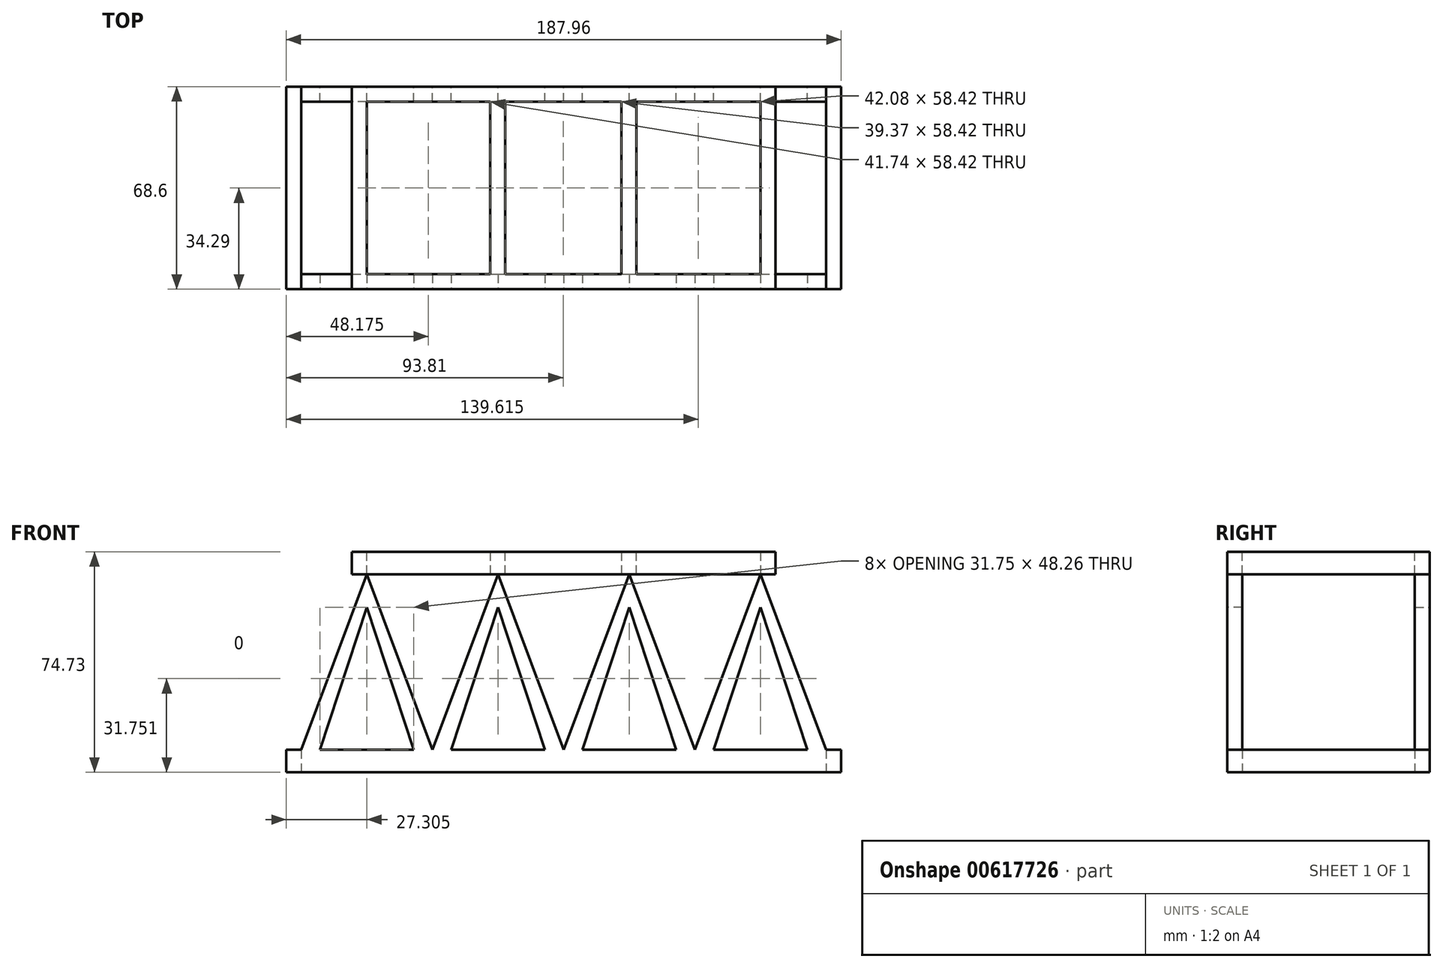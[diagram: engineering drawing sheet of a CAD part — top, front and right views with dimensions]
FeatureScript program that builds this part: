
annotation { "Feature Type Name" : "Feature", "Feature Type Description" : "" }
export const myFeature = defineFeature(function(context is Context, id is Id, definition is map)
    precondition{}
    {
        {
            var Q0;
            Q0=qCreatedBy(makeId("Front.planeOp"),FACE);
            var sketch = newSketch(context, id + "F0", { "sketchPlane" : qUnion([Q0])});
            skLineSegment(sketch, "E0.bottom", {"start": v(-88.9, -35.02) * mm, "end": v(88.9, -35.02) * mm});
            skLineSegment(sketch, "E0.top", {"start": v(-88.9, -42.64) * mm, "end": v(88.9, -42.64) * mm});
            skLineSegment(sketch, "E0.left", {"start": v(-88.9, -35.02) * mm, "end": v(-88.9, -42.64) * mm});
            skLineSegment(sketch, "E0.right", {"start": v(88.9, -35.02) * mm, "end": v(88.9, -42.64) * mm});
            skLineSegment(sketch, "E1.bottom", {"start": v(-66.68, 32.09) * mm, "end": v(66.68, 32.09) * mm});
            skLineSegment(sketch, "E1.top", {"start": v(-66.68, 24.47) * mm, "end": v(66.68, 24.47) * mm});
            skLineSegment(sketch, "E1.left", {"start": v(-66.68, 32.09) * mm, "end": v(-66.68, 24.47) * mm});
            skLineSegment(sketch, "E1.right", {"start": v(66.68, 32.09) * mm, "end": v(66.68, 24.47) * mm});
            skSolve(sketch);
        }
        {
            var Q0;
            Q0 = qSketchRegion(id + "F0", true);
            extrude(context, id + "F1", {"entities" : qUnion([Q0]), "oppositeDirection" : true, "depth" : 5.08 * mm, "offsetDistance" : 25.4 * mm});
        }
        {
            var Q0;
            Q0=qCreatedBy(makeId("Front.planeOp"),FACE);
            var sketch = newSketch(context, id + "F2", { "sketchPlane" : qUnion([Q0])});
            skLineSegment(sketch, "E2", {"start": v(-88.9, -35.02) * mm, "end": v(-66.67, 24.47) * mm});
            skLineSegment(sketch, "E3", {"start": v(-66.67, 24.47) * mm, "end": v(-44.45, -35.02) * mm});
            skLineSegment(sketch, "E4", {"start": v(-44.45, -35.02) * mm, "end": v(-88.9, -35.02) * mm});
            skLineSegment(sketch, "E5", {"start": v(-44.45, -35.02) * mm, "end": v(-22.22, 24.47) * mm});
            skLineSegment(sketch, "E6", {"start": v(-22.22, 24.47) * mm, "end": v(0, -35.02) * mm});
            skLineSegment(sketch, "E7", {"start": v(0, -35.02) * mm, "end": v(22.23, 24.47) * mm});
            skLineSegment(sketch, "E8", {"start": v(22.23, 24.47) * mm, "end": v(44.45, -35.02) * mm});
            skLineSegment(sketch, "E9", {"start": v(44.45, -35.02) * mm, "end": v(66.68, 24.47) * mm});
            skLineSegment(sketch, "E10", {"start": v(66.68, 24.47) * mm, "end": v(88.9, -35.02) * mm});
            skLineSegment(sketch, "E11", {"start": v(88.9, -35.02) * mm, "end": v(44.45, -35.02) * mm});
            skLineSegment(sketch, "E12", {"start": v(44.45, -35.02) * mm, "end": v(0, -35.02) * mm});
            skLineSegment(sketch, "E13", {"start": v(0, -35.02) * mm, "end": v(-44.45, -35.02) * mm});
            skLineSegment(sketch, "E14", {"start": v(-82.55, -35.02) * mm, "end": v(-88.9, -35.02) * mm});
            skLineSegment(sketch, "E15", {"start": v(-82.55, -35.02) * mm, "end": v(-66.68, 13.24) * mm});
            skLineSegment(sketch, "E16", {"start": v(-66.68, 13.24) * mm, "end": v(-50.8, -35.02) * mm});
            skLineSegment(sketch, "E17", {"start": v(-50.8, -35.02) * mm, "end": v(-44.45, -35.02) * mm});
            skLineSegment(sketch, "E18", {"start": v(-44.45, -35.02) * mm, "end": v(-38.1, -35.02) * mm});
            skLineSegment(sketch, "E19", {"start": v(-38.1, -35.02) * mm, "end": v(-22.23, 13.24) * mm});
            skLineSegment(sketch, "E20", {"start": v(-22.23, 13.24) * mm, "end": v(-6.35, -35.02) * mm});
            skLineSegment(sketch, "E21", {"start": v(-6.35, -35.02) * mm, "end": v(0, -35.02) * mm});
            skLineSegment(sketch, "E22", {"start": v(0, -35.02) * mm, "end": v(6.35, -35.02) * mm});
            skLineSegment(sketch, "E23", {"start": v(6.35, -35.02) * mm, "end": v(22.23, 13.24) * mm});
            skLineSegment(sketch, "E24", {"start": v(22.23, 13.24) * mm, "end": v(38.1, -35.02) * mm});
            skLineSegment(sketch, "E25", {"start": v(38.1, -35.02) * mm, "end": v(44.45, -35.02) * mm});
            skLineSegment(sketch, "E26", {"start": v(44.45, -35.02) * mm, "end": v(50.8, -35.02) * mm});
            skLineSegment(sketch, "E27", {"start": v(50.8, -35.02) * mm, "end": v(66.68, 13.24) * mm});
            skLineSegment(sketch, "E28", {"start": v(66.68, 13.24) * mm, "end": v(82.55, -35.02) * mm});
            skLineSegment(sketch, "E29", {"start": v(82.55, -35.02) * mm, "end": v(88.9, -35.02) * mm});
            skSolve(sketch);
        }
        {
            var Q0;
            Q0=makeQuery(id+"F2.imprint","IMPRINT",FACE,{"disambiguationData":[TD([[makeQuery(id+"F2.imprint","IMPRINT",EDGE,{"derivedFrom":sQuery(id+"F2.wireOp",EDGE,"E2")}),-1.0]])]});
            var Q1;
            Q1=makeQuery(id+"F2.imprint","IMPRINT",FACE,{"disambiguationData":[TD([[makeQuery(id+"F2.imprint","IMPRINT",EDGE,{"derivedFrom":sQuery(id+"F2.wireOp",EDGE,"E5")}),-1.0]])]});
            var Q2;
            Q2=makeQuery(id+"F2.imprint","IMPRINT",FACE,{"disambiguationData":[TD([[makeQuery(id+"F2.imprint","IMPRINT",EDGE,{"derivedFrom":sQuery(id+"F2.wireOp",EDGE,"E7")}),-1.0]])]});
            var Q3;
            Q3=makeQuery(id+"F2.imprint","IMPRINT",FACE,{"disambiguationData":[TD([[makeQuery(id+"F2.imprint","IMPRINT",EDGE,{"derivedFrom":sQuery(id+"F2.wireOp",EDGE,"E9")}),-1.0]])]});
            extrude(context, id + "F3", {"entities" : qUnion([Q0, Q1, Q2, Q3]), "operationType" : NewBodyOperationType.ADD, "oppositeDirection" : true, "depth" : 5.08 * mm, "offsetDistance" : 25.4 * mm});
        }
        {
            var Q0;
            Q0=makeQuery(id+"F1.opExtrude","SWEPT_FACE",FACE,{"disambiguationData":[OSD([sQuery(id+"F0.wireOp",EDGE,"E0.left")])]});
            var sketch = newSketch(context, id + "F4", { "sketchPlane" : qUnion([Q0])});
            skLineSegment(sketch, "E30", {"start": v(0, -42.64) * mm, "end": v(0, -35.02) * mm});
            skLineSegment(sketch, "E31", {"start": v(0, -35.02) * mm, "end": v(-63.5, -35.02) * mm});
            skLineSegment(sketch, "E32", {"start": v(-63.5, -35.02) * mm, "end": v(-63.5, -42.64) * mm});
            skLineSegment(sketch, "E33", {"start": v(-63.5, -42.64) * mm, "end": v(0, -42.64) * mm});
            skSolve(sketch);
        }
        {
            var Q0;
            {var subQ2=sQuery(id+"F4.wireOp",EDGE,"E32");Q0=makeQuery(id+"F4.imprint","IMPRINT",FACE,{"disambiguationData":[TD([[makeQuery(id+"F4.imprint","IMPRINT",EDGE,{"derivedFrom":subQ2}),1.0]])]});}
            var Q1;
            {var subQ0=sQuery(id+"F4.wireOp",EDGE,"E30");Q1=makeQuery(id+"F4.imprint","IMPRINT",FACE,{"disambiguationData":[TD([[makeQuery(id+"F4.imprint","IMPRINT",EDGE,{"derivedFrom":subQ0}),-1.0]])]});}
            extrude(context, id + "F5", {"entities" : qUnion([Q0, Q1]), "operationType" : NewBodyOperationType.ADD, "depth" : 5.08 * mm, "offsetDistance" : 25.4 * mm});
        }
        {
            var Q0;
            Q0=makeQuery(id+"F5.opExtrude","SWEPT_FACE",FACE,{"disambiguationData":[OSD([sQuery(id+"F4.wireOp",EDGE,"E32")])]});
            var sketch = newSketch(context, id + "F6", { "sketchPlane" : qUnion([Q0])});
            skLineSegment(sketch, "E34", {"start": v(93.98, -42.64) * mm, "end": v(-88.9, -42.64) * mm});
            skLineSegment(sketch, "E35", {"start": v(93.98, -42.64) * mm, "end": v(93.98, -35.02) * mm});
            skLineSegment(sketch, "E36", {"start": v(93.98, -35.02) * mm, "end": v(-88.9, -35.02) * mm});
            skLineSegment(sketch, "E37", {"start": v(-88.9, -35.02) * mm, "end": v(-88.9, -42.64) * mm});
            skSolve(sketch);
        }
        {
            var Q0;
            Q0 = qSketchRegion(id + "F6", true);
            extrude(context, id + "F7", {"entities" : qUnion([Q0]), "operationType" : NewBodyOperationType.ADD, "depth" : 5.08 * mm, "offsetDistance" : 25.4 * mm});
        }
        {
            var Q0;
            Q0=makeQuery(id+"F1.opExtrude","SWEPT_FACE",FACE,{"disambiguationData":[OSD([sQuery(id+"F0.wireOp",EDGE,"E0.right")])]});
            var sketch = newSketch(context, id + "F8", { "sketchPlane" : qUnion([Q0])});
            skLineSegment(sketch, "E38", {"start": v(0, -42.64) * mm, "end": v(0, -35.02) * mm});
            skLineSegment(sketch, "E39", {"start": v(0, -42.64) * mm, "end": v(68.6, -42.64) * mm});
            skPoint(sketch, "E39.endSnap0", {"position": v(2.54, -42.64) * mm});
            skLineSegment(sketch, "E40", {"start": v(68.6, -42.64) * mm, "end": v(68.6, -35.02) * mm});
            skLineSegment(sketch, "E41", {"start": v(68.6, -35.02) * mm, "end": v(0, -35.02) * mm});
            skSolve(sketch);
        }
        {
            var Q0;
            Q0 = qSketchRegion(id + "F8", true);
            extrude(context, id + "F9", {"entities" : qUnion([Q0]), "operationType" : NewBodyOperationType.ADD, "depth" : 5.08 * mm, "offsetDistance" : 25.4 * mm});
        }
        {
            var Q0;
            Q0=makeQuery(id+"F7.opExtrude","CAP_FACE",FACE,{"disambiguationData":[OSD([sQuery(id+"F6.wireOp",EDGE,"E34"),sQuery(id+"F6.wireOp",EDGE,"E35"),sQuery(id+"F6.wireOp",EDGE,"E36"),sQuery(id+"F6.wireOp",EDGE,"E37")])],"isStart":false});
            var sketch = newSketch(context, id + "F10", { "sketchPlane" : qUnion([Q0])});
            skLineSegment(sketch, "E42", {"start": v(-88.9, -35.02) * mm, "end": v(-66.67, 24.47) * mm});
            skLineSegment(sketch, "E43", {"start": v(-66.67, 24.47) * mm, "end": v(-44.45, -35.02) * mm});
            skLineSegment(sketch, "E44", {"start": v(-44.45, -35.02) * mm, "end": v(-88.9, -35.02) * mm});
            skLineSegment(sketch, "E45", {"start": v(-82.55, -35.02) * mm, "end": v(-66.68, 13.24) * mm});
            skLineSegment(sketch, "E46", {"start": v(-66.68, 13.24) * mm, "end": v(-50.8, -35.02) * mm});
            skLineSegment(sketch, "E47", {"start": v(-50.8, -35.02) * mm, "end": v(-44.45, -35.02) * mm});
            skLineSegment(sketch, "E48", {"start": v(-82.55, -35.02) * mm, "end": v(-88.9, -35.02) * mm});
            skLineSegment(sketch, "E49", {"start": v(-44.45, -35.02) * mm, "end": v(-22.22, 24.47) * mm});
            skLineSegment(sketch, "E50", {"start": v(-22.23, 24.47) * mm, "end": v(0, -35.02) * mm});
            skLineSegment(sketch, "E51", {"start": v(0, -35.02) * mm, "end": v(-6.35, -35.02) * mm});
            skLineSegment(sketch, "E52", {"start": v(-6.35, -35.02) * mm, "end": v(-22.23, 13.24) * mm});
            skLineSegment(sketch, "E53", {"start": v(-22.23, 13.24) * mm, "end": v(-38.1, -35.02) * mm});
            skLineSegment(sketch, "E54", {"start": v(-38.1, -35.02) * mm, "end": v(-44.45, -35.02) * mm});
            skLineSegment(sketch, "E55", {"start": v(0, -35.02) * mm, "end": v(22.23, 24.47) * mm});
            skLineSegment(sketch, "E56", {"start": v(22.22, 24.47) * mm, "end": v(44.45, -35.02) * mm});
            skLineSegment(sketch, "E57", {"start": v(44.45, -35.02) * mm, "end": v(38.1, -35.02) * mm});
            skLineSegment(sketch, "E58", {"start": v(38.1, -35.02) * mm, "end": v(22.22, 13.24) * mm});
            skLineSegment(sketch, "E59", {"start": v(22.22, 13.24) * mm, "end": v(6.35, -35.02) * mm});
            skLineSegment(sketch, "E60", {"start": v(6.35, -35.02) * mm, "end": v(0, -35.02) * mm});
            skLineSegment(sketch, "E61", {"start": v(44.45, -35.02) * mm, "end": v(66.67, 24.47) * mm});
            skLineSegment(sketch, "E62", {"start": v(66.67, 24.47) * mm, "end": v(88.9, -35.02) * mm});
            skLineSegment(sketch, "E63", {"start": v(88.9, -35.02) * mm, "end": v(82.55, -35.02) * mm});
            skLineSegment(sketch, "E64", {"start": v(82.55, -35.02) * mm, "end": v(66.68, 13.24) * mm});
            skLineSegment(sketch, "E65", {"start": v(66.68, 13.24) * mm, "end": v(50.8, -35.02) * mm});
            skLineSegment(sketch, "E66", {"start": v(50.8, -35.02) * mm, "end": v(44.45, -35.02) * mm});
            skSolve(sketch);
        }
        {
            var Q0;
            Q0=makeQuery(id+"F10.imprint","IMPRINT",FACE,{"disambiguationData":[TD([[makeQuery(id+"F10.imprint","IMPRINT",EDGE,{"derivedFrom":sQuery(id+"F10.wireOp",EDGE,"E42")}),-1.0]])]});
            var Q1;
            Q1=makeQuery(id+"F10.imprint","IMPRINT",FACE,{"disambiguationData":[TD([[makeQuery(id+"F10.imprint","IMPRINT",EDGE,{"derivedFrom":sQuery(id+"F10.wireOp",EDGE,"E49")}),-1.0]])]});
            var Q2;
            Q2=makeQuery(id+"F10.imprint","IMPRINT",FACE,{"disambiguationData":[TD([[makeQuery(id+"F10.imprint","IMPRINT",EDGE,{"derivedFrom":sQuery(id+"F10.wireOp",EDGE,"E55")}),-1.0]])]});
            var Q3;
            Q3=makeQuery(id+"F10.imprint","IMPRINT",FACE,{"disambiguationData":[TD([[makeQuery(id+"F10.imprint","IMPRINT",EDGE,{"derivedFrom":sQuery(id+"F10.wireOp",EDGE,"E61")}),-1.0]])]});
            extrude(context, id + "F11", {"entities" : qUnion([Q0, Q1, Q2, Q3]), "operationType" : NewBodyOperationType.ADD, "oppositeDirection" : true, "depth" : 5.08 * mm, "offsetDistance" : 25.4 * mm});
        }
        {
            var Q0;
            Q0=makeQuery(id+"F1.opExtrude","SWEPT_FACE",FACE,{"disambiguationData":[OSD([sQuery(id+"F0.wireOp",EDGE,"E1.right")])]});
            var sketch = newSketch(context, id + "F12", { "sketchPlane" : qUnion([Q0])});
            skLineSegment(sketch, "E67", {"start": v(0, 24.47) * mm, "end": v(63.5, 24.47) * mm});
            skPoint(sketch, "E67.endSnap0", {"position": v(2.54, 24.47) * mm});
            skLineSegment(sketch, "E68", {"start": v(0, 24.47) * mm, "end": v(0, 32.09) * mm});
            skLineSegment(sketch, "E69", {"start": v(63.5, 32.09) * mm, "end": v(63.5, 24.47) * mm});
            skLineSegment(sketch, "E70", {"start": v(63.5, 32.09) * mm, "end": v(0, 32.09) * mm});
            skSolve(sketch);
        }
        {
            var Q0;
            Q0 = qSketchRegion(id + "F12", true);
            extrude(context, id + "F13", {"entities" : qUnion([Q0]), "operationType" : NewBodyOperationType.ADD, "depth" : 5.08 * mm, "offsetDistance" : 25.4 * mm});
        }
        {
            var Q0;
            Q0=makeQuery(id+"F13.opExtrude","SWEPT_FACE",FACE,{"disambiguationData":[OSD([sQuery(id+"F12.wireOp",EDGE,"E69")])]});
            var sketch = newSketch(context, id + "F14", { "sketchPlane" : qUnion([Q0])});
            skLineSegment(sketch, "E71", {"start": v(-71.76, 24.47) * mm, "end": v(66.68, 24.47) * mm});
            skLineSegment(sketch, "E72", {"start": v(66.68, 24.47) * mm, "end": v(66.68, 32.09) * mm});
            skLineSegment(sketch, "E73", {"start": v(66.68, 32.09) * mm, "end": v(-71.76, 32.09) * mm});
            skLineSegment(sketch, "E74", {"start": v(-71.76, 32.09) * mm, "end": v(-71.76, 24.47) * mm});
            skSolve(sketch);
        }
        {
            var Q0;
            Q0 = qSketchRegion(id + "F14", true);
            extrude(context, id + "F15", {"entities" : qUnion([Q0]), "operationType" : NewBodyOperationType.ADD, "depth" : 5.08 * mm, "offsetDistance" : 25.4 * mm});
        }
        {
            var Q0;
            Q0=makeQuery(id+"F15.opExtrude","SWEPT_FACE",FACE,{"disambiguationData":[OSD([sQuery(id+"F14.wireOp",EDGE,"E72")])]});
            var sketch = newSketch(context, id + "F16", { "sketchPlane" : qUnion([Q0])});
            skLineSegment(sketch, "E75", {"start": v(-68.58, 24.47) * mm, "end": v(0, 24.47) * mm});
            skLineSegment(sketch, "E76", {"start": v(-68.58, 24.47) * mm, "end": v(-68.58, 32.09) * mm});
            skLineSegment(sketch, "E77", {"start": v(-68.58, 32.09) * mm, "end": v(0, 32.09) * mm});
            skLineSegment(sketch, "E78", {"start": v(0, 32.09) * mm, "end": v(0, 24.47) * mm});
            skSolve(sketch);
        }
        {
            var Q0;
            Q0 = qSketchRegion(id + "F16", true);
            extrude(context, id + "F17", {"entities" : qUnion([Q0]), "operationType" : NewBodyOperationType.ADD, "depth" : 5.08 * mm, "offsetDistance" : 25.4 * mm});
        }
        {
            var Q0;
            Q0=makeQuery(id+"F15.opExtrude","CAP_FACE",FACE,{"disambiguationData":[OSD([sQuery(id+"F14.wireOp",EDGE,"E71"),sQuery(id+"F14.wireOp",EDGE,"E72"),sQuery(id+"F14.wireOp",EDGE,"E73"),sQuery(id+"F14.wireOp",EDGE,"E74")])],"isStart":true});
            var sketch = newSketch(context, id + "F18", { "sketchPlane" : qUnion([Q0])});
            skLineSegment(sketch, "E79", {"start": v(-24.94, 32.09) * mm, "end": v(-24.94, 24.47) * mm});
            skLineSegment(sketch, "E80", {"start": v(-24.94, 24.47) * mm, "end": v(-19.86, 24.47) * mm});
            skLineSegment(sketch, "E81", {"start": v(-19.86, 24.47) * mm, "end": v(-19.86, 32.09) * mm});
            skLineSegment(sketch, "E82", {"start": v(-19.86, 32.09) * mm, "end": v(-24.94, 32.09) * mm});
            skSolve(sketch);
        }
        {
            var Q0;
            Q0 = qSketchRegion(id + "F18", true);
            extrude(context, id + "F19", {"entities" : qUnion([Q0]), "operationType" : NewBodyOperationType.ADD, "depth" : 63.5 * mm, "offsetDistance" : 25.4 * mm});
        }
        {
            var Q0;
            {var subQ0=sQuery(id+"F14.wireOp",EDGE,"E73");var subQ1=sQuery(id+"F14.wireOp",EDGE,"E71");Q0=makeQuery(id+"F19.boolean.opBoolean","SPLIT",FACE,{"disambiguationData":[TD([makeQuery(id+"F19.opExtrude","SWEPT_FACE",FACE,{"disambiguationData":[OSD([sQuery(id+"F18.wireOp",EDGE,"E81")])]})])],"derivedFrom":makeQuery(id+"F15.opExtrude","CAP_FACE",FACE,{"disambiguationData":[OSD([subQ1,sQuery(id+"F14.wireOp",EDGE,"E72"),subQ0,sQuery(id+"F14.wireOp",EDGE,"E74")])],"isStart":true})});}
            var sketch = newSketch(context, id + "F20", { "sketchPlane" : qUnion([Q0])});
            skLineSegment(sketch, "E83", {"start": v(19.51, 32.09) * mm, "end": v(19.51, 24.47) * mm});
            skLineSegment(sketch, "E84", {"start": v(19.51, 24.47) * mm, "end": v(24.6, 24.47) * mm});
            skLineSegment(sketch, "E85", {"start": v(24.6, 24.47) * mm, "end": v(24.6, 32.09) * mm});
            skLineSegment(sketch, "E86", {"start": v(24.6, 32.09) * mm, "end": v(19.51, 32.09) * mm});
            skSolve(sketch);
        }
        {
            var Q0;
            Q0 = qSketchRegion(id + "F20", true);
            extrude(context, id + "F21", {"entities" : qUnion([Q0]), "operationType" : NewBodyOperationType.ADD, "depth" : 63.5 * mm, "offsetDistance" : 25.4 * mm});
        }
    });
